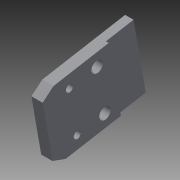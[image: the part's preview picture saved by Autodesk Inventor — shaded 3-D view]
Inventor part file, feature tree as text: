
AUTODESK INVENTOR PART (.ipt)
format: ipt  version: 2013 (Build 170138000, 138)  size: 188,416 bytes
history: native  units: mm
features: sketch x7, extrude x4, hole x4, other x2, pattern_circular x1
ambient origin geometry x8: Origin, YZ Plane, XZ Plane, XY Plane, X Axis, Y Axis, Z Axis, Center Point
feature tree (18):
  other  "ソリッド1"
  extrude  "押し出し1"  Depth=20.0mm
  hole  "穴2"  [1 undecoded]
  extrude  "押し出し2"  Depth=10.0mm
  hole  "穴3"  [1 undecoded]
  hole  "穴4"  [1 undecoded]
  pattern_circular  "円形状パターン3"  [2 undecoded]
  extrude  "押し出し3"  Depth=8.0mm
  hole  "穴5"  [1 undecoded]
  extrude  "押し出し4"  Depth=4.0mm
  sketch  "スケッチ4"
  sketch  "スケッチ5"
  sketch  "スケッチ6"
  sketch  "スケッチ7"
  sketch  "スケッチ8"
  sketch  "スケッチ9"
  sketch  "スケッチ10"
  other  "断面エッジを投影1"
note: 6 required parameter values undecoded (feature->parameter linkage not recoverable at this tier; creation-order binding heuristic only, values carry confidence <= 0.55)
